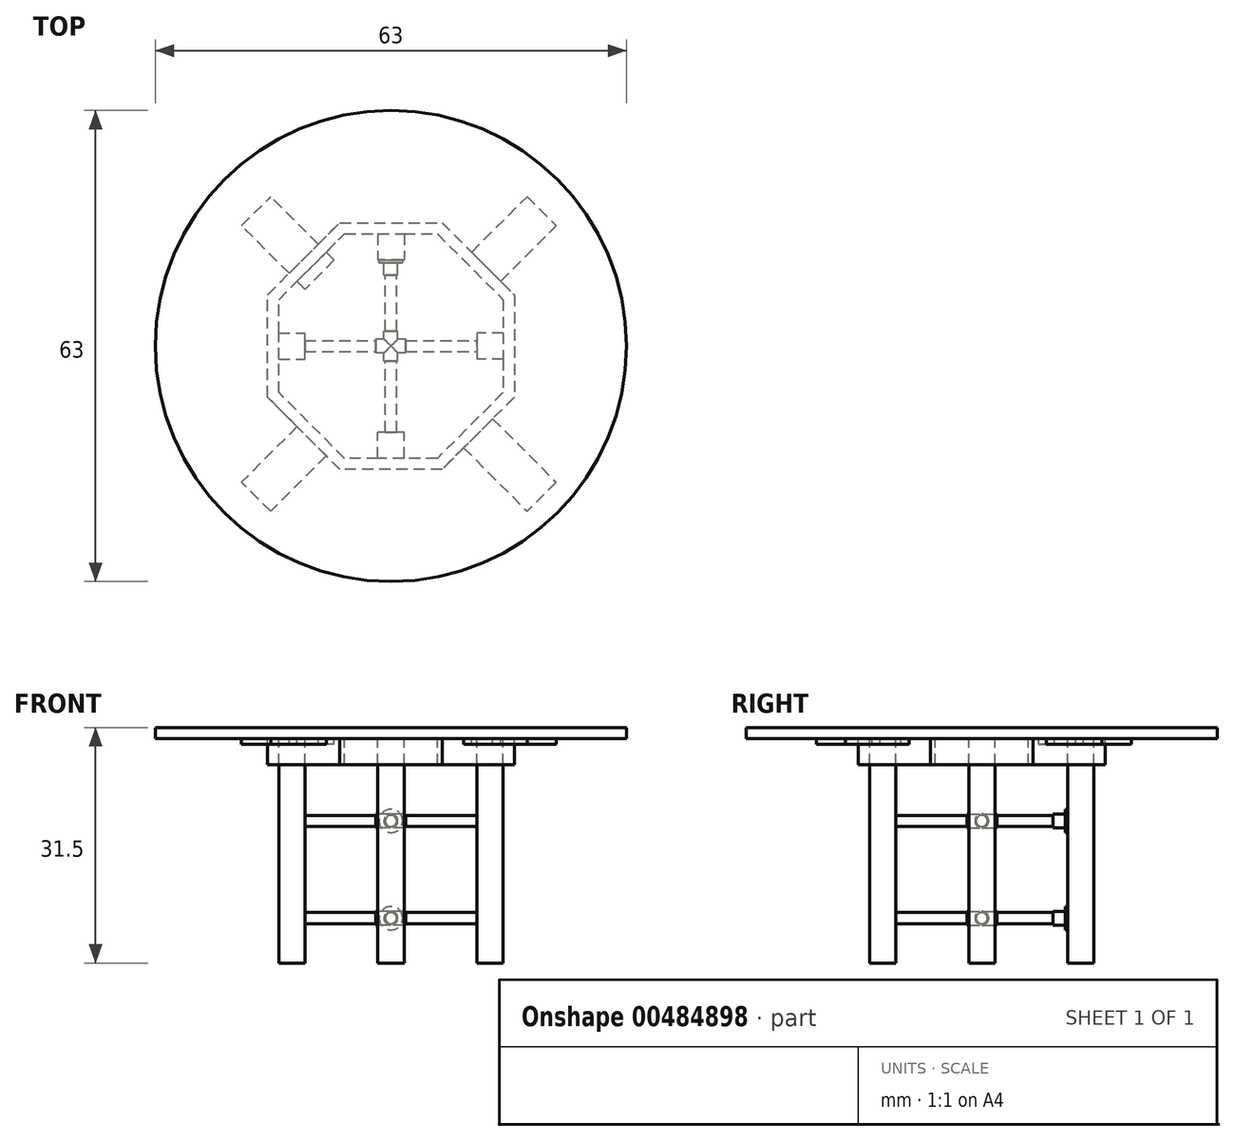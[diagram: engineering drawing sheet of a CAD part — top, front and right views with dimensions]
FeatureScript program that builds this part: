
annotation { "Feature Type Name" : "Feature", "Feature Type Description" : "" }
export const myFeature = defineFeature(function(context is Context, id is Id, definition is map)
    precondition{}
    {
        {
            var Q0;
            Q0=qCreatedBy(makeId("Top.planeOp"),FACE);
            var sketch = newSketch(context, id + "F0", { "sketchPlane" : qUnion([Q0])});
            skCircle(sketch, "E0", {"center": v(0, 0) * mm, "radius": 31.5 * mm});
            skSolve(sketch);
        }
        {
            var Q0;
            Q0=makeQuery(id+"F0.imprint","IMPRINT",FACE,{"disambiguationData":[TD([[makeQuery(id+"F0.imprint","IMPRINT",EDGE,{"derivedFrom":sQuery(id+"F0.wireOp",EDGE,"E0")}),1.0]])]});
            extrude(context, id + "F1", {"entities" : qUnion([Q0]), "depth" : 1.5 * mm, "offsetDistance" : 25 * mm});
        }
        {
            var Q0;
            Q0=qCreatedBy(makeId("Top.planeOp"),FACE);
            var sketch = newSketch(context, id + "F2", { "sketchPlane" : qUnion([Q0])});
            skCircle(sketch, "E1.cCircle", {"center": v(0, 0) * mm, "radius": 15 * mm, "construction": true});
            skLineSegment(sketch, "E1.0", {"start": v(-6.21, -15) * mm, "end": v(-15, -6.21) * mm});
            skLineSegment(sketch, "E1.1", {"start": v(-15, -6.21) * mm, "end": v(-15, 6.21) * mm});
            skLineSegment(sketch, "E1.2", {"start": v(-15, 6.21) * mm, "end": v(-6.21, 15) * mm});
            skLineSegment(sketch, "E1.3", {"start": v(-6.21, 15) * mm, "end": v(6.21, 15) * mm});
            skLineSegment(sketch, "E1.4", {"start": v(6.21, 15) * mm, "end": v(15, 6.21) * mm});
            skLineSegment(sketch, "E1.5", {"start": v(15, 6.21) * mm, "end": v(15, -6.21) * mm});
            skLineSegment(sketch, "E1.6", {"start": v(15, -6.21) * mm, "end": v(6.21, -15) * mm});
            skLineSegment(sketch, "E1.7", {"start": v(6.21, -15) * mm, "end": v(-6.21, -15) * mm});
            skPoint(sketch, "E1.0.midPoint", {"position": v(-10.6, -10.6) * mm});
            skLineSegment(sketch, "E2.0", {"start": v(-16.5, 6.83) * mm, "end": v(-6.83, 16.5) * mm});
            skLineSegment(sketch, "E2.1", {"start": v(-16.5, -6.83) * mm, "end": v(-16.5, 6.83) * mm});
            skLineSegment(sketch, "E2.2", {"start": v(-6.83, 16.5) * mm, "end": v(6.83, 16.5) * mm});
            skLineSegment(sketch, "E2.3", {"start": v(-6.83, -16.5) * mm, "end": v(-16.5, -6.83) * mm});
            skLineSegment(sketch, "E2.4", {"start": v(6.83, 16.5) * mm, "end": v(16.5, 6.83) * mm});
            skLineSegment(sketch, "E2.5", {"start": v(16.5, 6.83) * mm, "end": v(16.5, -6.83) * mm});
            skLineSegment(sketch, "E2.6", {"start": v(16.5, -6.83) * mm, "end": v(6.83, -16.5) * mm});
            skLineSegment(sketch, "E2.7", {"start": v(6.83, -16.5) * mm, "end": v(-6.83, -16.5) * mm});
            skSolve(sketch);
        }
        {
            var Q0;
            Q0=makeQuery(id+"F2.imprint","IMPRINT",FACE,{"disambiguationData":[TD([[makeQuery(id+"F2.imprint","IMPRINT",EDGE,{"derivedFrom":sQuery(id+"F2.wireOp",EDGE,"E1.0")}),1.0]])]});
            extrude(context, id + "F3", {"entities" : qUnion([Q0]), "operationType" : NewBodyOperationType.ADD, "oppositeDirection" : true, "depth" : 3.5 * mm, "offsetDistance" : 25 * mm});
        }
        {
            var Q0;
            Q0=qCreatedBy(makeId("Top.planeOp"),FACE);
            var sketch = newSketch(context, id + "F4", { "sketchPlane" : qUnion([Q0])});
            skLineSegment(sketch, "E3.bottom", {"start": v(-1.75, 15) * mm, "end": v(1.75, 15) * mm});
            skLineSegment(sketch, "E3.top", {"start": v(-1.75, 11.5) * mm, "end": v(1.75, 11.5) * mm});
            skLineSegment(sketch, "E3.left", {"start": v(-1.75, 15) * mm, "end": v(-1.75, 11.5) * mm});
            skLineSegment(sketch, "E3.right", {"start": v(1.75, 15) * mm, "end": v(1.75, 11.5) * mm});
            skLineSegment(sketch, "E4.1.0", {"start": v(-15, -1.75) * mm, "end": v(-11.5, -1.75) * mm});
            skLineSegment(sketch, "E4.1.1", {"start": v(-15, -1.75) * mm, "end": v(-15, 1.75) * mm});
            skLineSegment(sketch, "E4.1.2", {"start": v(-15, 1.75) * mm, "end": v(-11.5, 1.75) * mm});
            skLineSegment(sketch, "E4.1.3", {"start": v(-11.5, -1.75) * mm, "end": v(-11.5, 1.75) * mm});
            skLineSegment(sketch, "E4.2.0", {"start": v(1.75, -15) * mm, "end": v(1.75, -11.5) * mm});
            skLineSegment(sketch, "E4.2.1", {"start": v(1.75, -15) * mm, "end": v(-1.75, -15) * mm});
            skLineSegment(sketch, "E4.2.2", {"start": v(-1.75, -15) * mm, "end": v(-1.75, -11.5) * mm});
            skLineSegment(sketch, "E4.2.3", {"start": v(1.75, -11.5) * mm, "end": v(-1.75, -11.5) * mm});
            skPoint(sketch, "E4.center", {"position": v(0, 0) * mm});
            skLineSegment(sketch, "E5.2.3.0", {"start": v(15, 1.75) * mm, "end": v(11.5, 1.75) * mm});
            skLineSegment(sketch, "E5.3.3.0", {"start": v(15, 1.75) * mm, "end": v(15, -1.75) * mm});
            skLineSegment(sketch, "E5.6.3.0", {"start": v(15, -1.75) * mm, "end": v(11.5, -1.75) * mm});
            skLineSegment(sketch, "E5.9.3.0", {"start": v(11.5, 1.75) * mm, "end": v(11.5, -1.75) * mm});
            skSolve(sketch);
        }
        {
            var Q0;
            Q0=makeQuery(id+"F4.imprint","IMPRINT",FACE,{"disambiguationData":[TD([[makeQuery(id+"F4.imprint","IMPRINT",EDGE,{"derivedFrom":sQuery(id+"F4.wireOp",EDGE,"E4.2.0")}),1.0]])]});
            var Q1;
            Q1=makeQuery(id+"F4.imprint","IMPRINT",FACE,{"disambiguationData":[TD([[makeQuery(id+"F4.imprint","IMPRINT",EDGE,{"derivedFrom":sQuery(id+"F4.wireOp",EDGE,"E5.2.3.0")}),1.0]])]});
            var Q2;
            Q2=makeQuery(id+"F4.imprint","IMPRINT",FACE,{"disambiguationData":[TD([[makeQuery(id+"F4.imprint","IMPRINT",EDGE,{"derivedFrom":sQuery(id+"F4.wireOp",EDGE,"E3.bottom")}),-1.0]])]});
            var Q3;
            Q3=makeQuery(id+"F4.imprint","IMPRINT",FACE,{"disambiguationData":[TD([[makeQuery(id+"F4.imprint","IMPRINT",EDGE,{"derivedFrom":sQuery(id+"F4.wireOp",EDGE,"E4.1.0")}),1.0]])]});
            extrude(context, id + "F5", {"entities" : qUnion([Q0, Q1, Q2, Q3]), "operationType" : NewBodyOperationType.ADD, "oppositeDirection" : true, "depth" : 30 * mm, "offsetDistance" : 25 * mm});
        }
        {
            var Q0;
            Q0=makeQuery(id+"F5.opExtrude","SWEPT_FACE",FACE,{"disambiguationData":[OSD([sQuery(id+"F4.wireOp",EDGE,"E3.top")])]});
            var sketch = newSketch(context, id + "F6", { "sketchPlane" : qUnion([Q0])});
            skCircle(sketch, "E6", {"center": v(0, -24) * mm, "radius": 0.75 * mm});
            skCircle(sketch, "E7", {"center": v(0, -11) * mm, "radius": 0.75 * mm});
            skCircle(sketch, "E8", {"center": v(0, -11) * mm, "radius": 0.93 * mm});
            skCircle(sketch, "E9", {"center": v(0, -11) * mm, "radius": 1.56 * mm});
            skCircle(sketch, "E10", {"center": v(0, -24) * mm, "radius": 0.93 * mm});
            skCircle(sketch, "E11", {"center": v(0, -24) * mm, "radius": 1.56 * mm});
            skSolve(sketch);
        }
        {
            var Q0;
            Q0=makeQuery(id+"F6.imprint","IMPRINT",FACE,{"disambiguationData":[TD([[makeQuery(id+"F6.imprint","IMPRINT",EDGE,{"derivedFrom":sQuery(id+"F6.wireOp",EDGE,"E7")}),1.0]])]});
            var Q1;
            Q1=makeQuery(id+"F6.imprint","IMPRINT",FACE,{"disambiguationData":[TD([[makeQuery(id+"F6.imprint","IMPRINT",EDGE,{"derivedFrom":sQuery(id+"F6.wireOp",EDGE,"E6")}),1.0]])]});
            extrude(context, id + "F7", {"entities" : qUnion([Q0, Q1]), "operationType" : NewBodyOperationType.ADD, "endBound" : BoundingType.UP_TO_NEXT, "depth" : 25 * mm, "offsetDistance" : 25 * mm});
        }
        {
            var Q0;
            Q0=makeQuery(id+"F5.opExtrude","SWEPT_FACE",FACE,{"disambiguationData":[OSD([sQuery(id+"F4.wireOp",EDGE,"E5.9.3.0")])]});
            var sketch = newSketch(context, id + "F8", { "sketchPlane" : qUnion([Q0])});
            skCircle(sketch, "E12", {"center": v(0, -24) * mm, "radius": 0.75 * mm});
            skCircle(sketch, "E13", {"center": v(0, -11) * mm, "radius": 0.75 * mm});
            skSolve(sketch);
        }
        {
            var Q0;
            Q0=makeQuery(id+"F8.imprint","IMPRINT",FACE,{"disambiguationData":[TD([[makeQuery(id+"F8.imprint","IMPRINT",EDGE,{"derivedFrom":sQuery(id+"F8.wireOp",EDGE,"E12")}),1.0]])]});
            var Q1;
            Q1=makeQuery(id+"F8.imprint","IMPRINT",FACE,{"disambiguationData":[TD([[makeQuery(id+"F8.imprint","IMPRINT",EDGE,{"derivedFrom":sQuery(id+"F8.wireOp",EDGE,"E13")}),1.0]])]});
            var Q2;
            Q2=makeQuery(id+"F5.opExtrude","SWEPT_FACE",FACE,{"disambiguationData":[OSD([sQuery(id+"F4.wireOp",EDGE,"E4.1.3")])]});
            extrude(context, id + "F9", {"entities" : qUnion([Q0, Q1]), "operationType" : NewBodyOperationType.ADD, "endBound" : BoundingType.UP_TO_SURFACE, "depth" : 25 * mm, "endBoundEntityFace" : qUnion([Q2]), "offsetDistance" : 25 * mm});
        }
        {
            var Q0;
            Q0=qCreatedBy(makeId("Front.planeOp"),FACE);
            var sketch = newSketch(context, id + "F10", { "sketchPlane" : qUnion([Q0])});
            skCircle(sketch, "E14", {"center": v(0, -24) * mm, "radius": 0.93 * mm});
            skCircle(sketch, "E15", {"center": v(0, -11) * mm, "radius": 0.93 * mm});
            skSolve(sketch);
        }
        {
            var Q0;
            Q0=makeQuery(id+"F10.imprint","IMPRINT",FACE,{"disambiguationData":[TD([[makeQuery(id+"F10.imprint","IMPRINT",EDGE,{"derivedFrom":sQuery(id+"F10.wireOp",EDGE,"E15")}),1.0]])]});
            var Q1;
            Q1=makeQuery(id+"F10.imprint","IMPRINT",FACE,{"disambiguationData":[TD([[makeQuery(id+"F10.imprint","IMPRINT",EDGE,{"derivedFrom":sQuery(id+"F10.wireOp",EDGE,"E14")}),1.0]])]});
            extrude(context, id + "F11", {"entities" : qUnion([Q0, Q1]), "operationType" : NewBodyOperationType.ADD, "endBound" : BoundingType.SYMMETRIC, "depth" : 4 * mm, "offsetDistance" : 25 * mm});
        }
        {
            var Q0;
            Q0=qCreatedBy(makeId("Right.planeOp"),FACE);
            var sketch = newSketch(context, id + "F12", { "sketchPlane" : qUnion([Q0])});
            skCircle(sketch, "E16", {"center": v(0, -24) * mm, "radius": 0.93 * mm});
            skCircle(sketch, "E17", {"center": v(0, -11) * mm, "radius": 0.93 * mm});
            skSolve(sketch);
        }
        {
            var Q0;
            Q0 = qSketchRegion(id + "F12", true);
            extrude(context, id + "F13", {"entities" : qUnion([Q0]), "operationType" : NewBodyOperationType.ADD, "endBound" : BoundingType.SYMMETRIC, "depth" : 4 * mm, "offsetDistance" : 25 * mm});
        }
        {
            var Q0;
            Q0=makeQuery(id+"F6.imprint","IMPRINT",FACE,{"disambiguationData":[TD([[makeQuery(id+"F6.imprint","IMPRINT",EDGE,{"derivedFrom":sQuery(id+"F6.wireOp",EDGE,"E6")}),-1.0]])]});
            var Q1;
            Q1=makeQuery(id+"F6.imprint","IMPRINT",FACE,{"disambiguationData":[TD([[makeQuery(id+"F6.imprint","IMPRINT",EDGE,{"derivedFrom":sQuery(id+"F6.wireOp",EDGE,"E7")}),-1.0]])]});
            extrude(context, id + "F14", {"entities" : qUnion([Q0, Q1]), "operationType" : NewBodyOperationType.ADD, "depth" : 2 * mm, "offsetDistance" : 25 * mm});
        }
        {
            var Q0;
            Q0=makeQuery(id+"F6.imprint","IMPRINT",FACE,{"disambiguationData":[TD([[makeQuery(id+"F6.imprint","IMPRINT",EDGE,{"derivedFrom":sQuery(id+"F6.wireOp",EDGE,"E10")}),-1.0]])]});
            var Q1;
            Q1=makeQuery(id+"F6.imprint","IMPRINT",FACE,{"disambiguationData":[TD([[makeQuery(id+"F6.imprint","IMPRINT",EDGE,{"derivedFrom":sQuery(id+"F6.wireOp",EDGE,"E8")}),-1.0]])]});
            extrude(context, id + "F15", {"entities" : qUnion([Q0, Q1]), "operationType" : NewBodyOperationType.ADD, "depth" : 0.35 * mm, "offsetDistance" : 25 * mm});
        }
        {
            var Q0;
            {var subQ0=sQuery(id+"F0.wireOp",EDGE,"E0");Q0=makeQuery(id+"F3.boolean.opBoolean","SPLIT",FACE,{"disambiguationData":[TD([makeQuery(id+"F1.opExtrude","SWEPT_FACE",FACE,{"disambiguationData":[OSD([subQ0])]})])],"derivedFrom":makeQuery(id+"F1.opExtrude","CAP_FACE",FACE,{"disambiguationData":[OSD([subQ0])],"isStart":true})});}
            var sketch = newSketch(context, id + "F16", { "sketchPlane" : qUnion([Q0])});
            skLineSegment(sketch, "E18.0", {"start": v(13.61, 9.72) * mm, "end": v(22.1, 18.2) * mm});
            skLineSegment(sketch, "E19.0", {"start": v(9.72, 13.61) * mm, "end": v(18.2, 22.1) * mm});
            skLineSegment(sketch, "E20.0", {"start": v(22.1, 18.2) * mm, "end": v(18.2, 22.1) * mm});
            skLineSegment(sketch, "E21", {"start": v(9.72, 13.61) * mm, "end": v(13.61, 9.72) * mm});
            skLineSegment(sketch, "E22.1.0", {"start": v(-11.5, 9.72) * mm, "end": v(-19.98, 18.2) * mm});
            skLineSegment(sketch, "E22.1.1", {"start": v(-16.09, 22.1) * mm, "end": v(-19.98, 18.2) * mm});
            skLineSegment(sketch, "E22.1.2", {"start": v(-7.6, 13.61) * mm, "end": v(-16.09, 22.1) * mm});
            skLineSegment(sketch, "E22.1.3", {"start": v(-11.5, 9.72) * mm, "end": v(-7.6, 13.61) * mm});
            skLineSegment(sketch, "E22.2.0", {"start": v(-7.6, -11.5) * mm, "end": v(-16.09, -19.98) * mm});
            skLineSegment(sketch, "E22.2.1", {"start": v(-19.98, -16.09) * mm, "end": v(-16.09, -19.98) * mm});
            skLineSegment(sketch, "E22.2.2", {"start": v(-11.5, -7.6) * mm, "end": v(-19.98, -16.09) * mm});
            skLineSegment(sketch, "E22.2.3", {"start": v(-7.6, -11.5) * mm, "end": v(-11.5, -7.6) * mm});
            skLineSegment(sketch, "E22.3.0", {"start": v(13.61, -7.6) * mm, "end": v(22.1, -16.09) * mm});
            skLineSegment(sketch, "E22.3.1", {"start": v(18.2, -19.98) * mm, "end": v(22.1, -16.09) * mm});
            skLineSegment(sketch, "E22.3.2", {"start": v(9.72, -11.5) * mm, "end": v(18.2, -19.98) * mm});
            skLineSegment(sketch, "E22.3.3", {"start": v(13.61, -7.6) * mm, "end": v(9.72, -11.5) * mm});
            skPoint(sketch, "E22.center", {"position": v(1.06, 1.06) * mm});
            skSolve(sketch);
        }
        {
            var Q0;
            Q0 = qSketchRegion(id + "F16", true);
            extrude(context, id + "F17", {"entities" : qUnion([Q0]), "operationType" : NewBodyOperationType.ADD, "depth" : 0.75 * mm, "offsetDistance" : 25 * mm});
        }
    });
